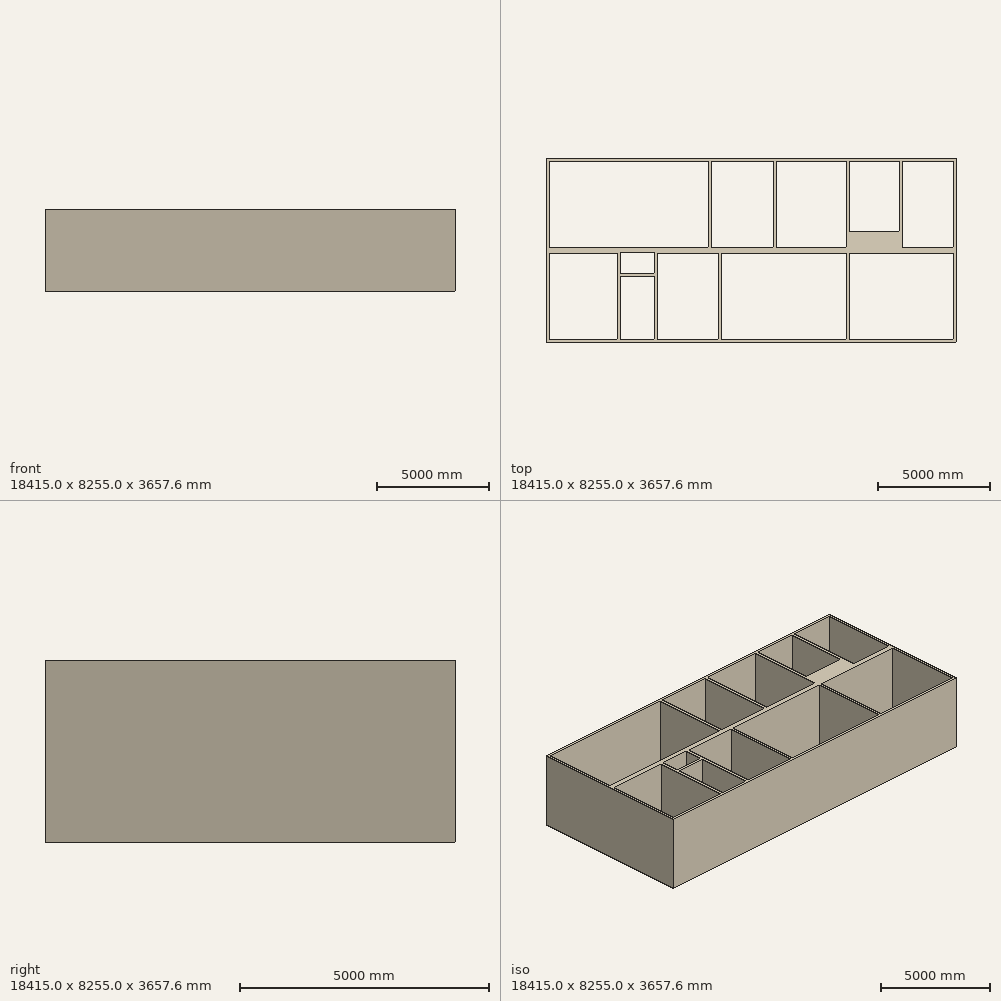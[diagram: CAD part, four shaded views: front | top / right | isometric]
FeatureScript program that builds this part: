
annotation { "Feature Type Name" : "Feature", "Feature Type Description" : "" }
export const myFeature = defineFeature(function(context is Context, id is Id, definition is map)
    precondition{}
    {
        {
            var Q0;
            Q0=qCreatedBy(makeId("Top.planeOp"),FACE);
            var sketch = newSketch(context, id + "F0", { "sketchPlane" : qUnion([Q0])});
            skLineSegment(sketch, "E0.bottom", {"start": v(0, 0) * mm, "end": v(3073.4, 0) * mm});
            skLineSegment(sketch, "E0.top", {"start": v(0, 3860.8) * mm, "end": v(3073.4, 3860.8) * mm});
            skLineSegment(sketch, "E0.left", {"start": v(0, 0) * mm, "end": v(0, 3860.8) * mm});
            skLineSegment(sketch, "E0.right", {"start": v(3073.4, 0) * mm, "end": v(3073.4, 3860.8) * mm});
            skLineSegment(sketch, "E1.bottom", {"start": v(3208.87, 0) * mm, "end": v(4732.87, 0) * mm});
            skLineSegment(sketch, "E1.top", {"start": v(3208.87, 2819.4) * mm, "end": v(4732.87, 2819.4) * mm});
            skLineSegment(sketch, "E1.left", {"start": v(3208.87, 0) * mm, "end": v(3208.87, 2819.4) * mm});
            skLineSegment(sketch, "E1.right", {"start": v(4732.87, 0) * mm, "end": v(4732.87, 2819.4) * mm});
            skLineSegment(sketch, "E2.bottom", {"start": v(3208.87, 2954.87) * mm, "end": v(4732.87, 2954.87) * mm});
            skLineSegment(sketch, "E2.top", {"start": v(3208.87, 3894.67) * mm, "end": v(4732.87, 3894.67) * mm});
            skLineSegment(sketch, "E2.left", {"start": v(3208.87, 2954.87) * mm, "end": v(3208.87, 3894.67) * mm});
            skLineSegment(sketch, "E2.right", {"start": v(4732.87, 2954.87) * mm, "end": v(4732.87, 3894.67) * mm});
            skLineSegment(sketch, "E3.bottom", {"start": v(4868.33, 0) * mm, "end": v(7611.53, 0) * mm});
            skLineSegment(sketch, "E3.top", {"start": v(4868.33, 3860.8) * mm, "end": v(7611.53, 3860.8) * mm});
            skLineSegment(sketch, "E3.left", {"start": v(4868.33, 0) * mm, "end": v(4868.33, 3860.8) * mm});
            skLineSegment(sketch, "E3.right", {"start": v(7611.53, 0) * mm, "end": v(7611.53, 3860.8) * mm});
            skLineSegment(sketch, "E4.bottom", {"start": v(7747, 0) * mm, "end": v(13360.4, 0) * mm});
            skLineSegment(sketch, "E4.top", {"start": v(7747, 3860.8) * mm, "end": v(13360.4, 3860.8) * mm});
            skLineSegment(sketch, "E4.left", {"start": v(7747, 0) * mm, "end": v(7747, 3860.8) * mm});
            skLineSegment(sketch, "E4.right", {"start": v(13360.4, 0) * mm, "end": v(13360.4, 3860.8) * mm});
            skLineSegment(sketch, "E5.bottom", {"start": v(13495.87, 0) * mm, "end": v(18144.07, 0) * mm});
            skLineSegment(sketch, "E5.top", {"start": v(13495.87, 3860.8) * mm, "end": v(18144.07, 3860.8) * mm});
            skLineSegment(sketch, "E5.left", {"start": v(13495.87, 0) * mm, "end": v(13495.87, 3860.8) * mm});
            skLineSegment(sketch, "E5.right", {"start": v(18144.07, 0) * mm, "end": v(18144.07, 3860.8) * mm});
            skLineSegment(sketch, "E6.bottom", {"start": v(18144.07, 4123.27) * mm, "end": v(15858.07, 4123.27) * mm});
            skLineSegment(sketch, "E6.top", {"start": v(18144.07, 7984.07) * mm, "end": v(15858.07, 7984.07) * mm});
            skLineSegment(sketch, "E6.left", {"start": v(18144.07, 4123.27) * mm, "end": v(18144.07, 7984.07) * mm});
            skLineSegment(sketch, "E6.right", {"start": v(15858.07, 4123.27) * mm, "end": v(15858.07, 7984.07) * mm});
            skLineSegment(sketch, "E7.bottom", {"start": v(15722.6, 7984.07) * mm, "end": v(13487.4, 7984.07) * mm});
            skLineSegment(sketch, "E7.top", {"start": v(15722.6, 4841.01) * mm, "end": v(13487.4, 4841.01) * mm});
            skLineSegment(sketch, "E7.left", {"start": v(15722.6, 7984.07) * mm, "end": v(15722.6, 4841.01) * mm});
            skLineSegment(sketch, "E7.right", {"start": v(13487.4, 7984.07) * mm, "end": v(13487.4, 4841.01) * mm});
            skLineSegment(sketch, "E8.bottom", {"start": v(13351.93, 7984.07) * mm, "end": v(10202.33, 7984.07) * mm});
            skLineSegment(sketch, "E8.top", {"start": v(13351.93, 4123.27) * mm, "end": v(10202.33, 4123.27) * mm});
            skLineSegment(sketch, "E8.left", {"start": v(13351.93, 7984.07) * mm, "end": v(13351.93, 4123.27) * mm});
            skLineSegment(sketch, "E8.right", {"start": v(10202.33, 7984.07) * mm, "end": v(10202.33, 4123.27) * mm});
            skLineSegment(sketch, "E9.bottom", {"start": v(10066.87, 7984.07) * mm, "end": v(7272.87, 7984.07) * mm});
            skLineSegment(sketch, "E9.top", {"start": v(10066.87, 4123.27) * mm, "end": v(7272.87, 4123.27) * mm});
            skLineSegment(sketch, "E9.left", {"start": v(10066.87, 7984.07) * mm, "end": v(10066.87, 4123.27) * mm});
            skLineSegment(sketch, "E9.right", {"start": v(7272.87, 7984.07) * mm, "end": v(7272.87, 4123.27) * mm});
            skLineSegment(sketch, "E10.bottom", {"start": v(7137.4, 7984.07) * mm, "end": v(0, 7984.07) * mm});
            skLineSegment(sketch, "E10.top", {"start": v(7137.4, 4123.27) * mm, "end": v(0, 4123.27) * mm});
            skLineSegment(sketch, "E10.left", {"start": v(7137.4, 7984.07) * mm, "end": v(7137.4, 4123.27) * mm});
            skLineSegment(sketch, "E10.right", {"start": v(0, 7984.07) * mm, "end": v(0, 4123.27) * mm});
            skLineSegment(sketch, "E11", {"start": v(3073.4, 0) * mm, "end": v(3208.87, 0) * mm});
            skLineSegment(sketch, "E12", {"start": v(4732.87, 0) * mm, "end": v(4868.33, 0) * mm});
            skLineSegment(sketch, "E13", {"start": v(7611.53, 0) * mm, "end": v(7747, 0) * mm});
            skLineSegment(sketch, "E14", {"start": v(13360.4, 0) * mm, "end": v(13495.87, 0) * mm});
            skLineSegment(sketch, "E15.bottom", {"start": v(-135.47, -135.47) * mm, "end": v(18279.53, -135.47) * mm});
            skLineSegment(sketch, "E15.top", {"start": v(-135.47, 8119.53) * mm, "end": v(18279.53, 8119.53) * mm});
            skLineSegment(sketch, "E15.left", {"start": v(-135.47, -135.47) * mm, "end": v(-135.47, 8119.53) * mm});
            skLineSegment(sketch, "E15.right", {"start": v(18279.53, -135.47) * mm, "end": v(18279.53, 8119.53) * mm});
            skLineSegment(sketch, "E16", {"start": v(3208.87, 2954.87) * mm, "end": v(3208.87, 2819.4) * mm});
            skLineSegment(sketch, "E17", {"start": v(7137.4, 7984.07) * mm, "end": v(7272.87, 7984.07) * mm});
            skLineSegment(sketch, "E18", {"start": v(10066.87, 7984.07) * mm, "end": v(10202.33, 7984.07) * mm});
            skLineSegment(sketch, "E19", {"start": v(13351.93, 7984.07) * mm, "end": v(13487.4, 7984.07) * mm});
            skLineSegment(sketch, "E20", {"start": v(15722.6, 7984.07) * mm, "end": v(15858.07, 7984.07) * mm});
            skLineSegment(sketch, "E21", {"start": v(0, 0) * mm, "end": v(-135.47, 0) * mm});
            skLineSegment(sketch, "E22", {"start": v(0, -135.47) * mm, "end": v(0, 0) * mm});
            skLineSegment(sketch, "E23", {"start": v(0, 7984.07) * mm, "end": v(0, 8119.53) * mm});
            skLineSegment(sketch, "E24", {"start": v(18144.07, 0) * mm, "end": v(18279.53, 0) * mm});
            skSolve(sketch);
        }
        {
            var Q0;
            Q0=makeQuery(id+"F0.imprint","IMPRINT",FACE,{"disambiguationData":[TD([[makeQuery(id+"F0.imprint","IMPRINT",EDGE,{"derivedFrom":sQuery(id+"F0.wireOp",EDGE,"E0.top")}),1.0]])]});
            var Q1;
            {var subQ4=sQuery(id+"F0.wireOp",EDGE,"E21");Q1=makeQuery(id+"F0.imprint","IMPRINT",FACE,{"disambiguationData":[TD([[makeQuery(id+"F0.imprint","IMPRINT",EDGE,{"derivedFrom":subQ4}),1.0]])]});}
            var Q2;
            Q2=makeQuery(id+"F0.imprint","IMPRINT",FACE,{"disambiguationData":[TD([[makeQuery(id+"F0.imprint","IMPRINT",EDGE,{"derivedFrom":sQuery(id+"F0.wireOp",EDGE,"E0.bottom")}),-1.0]])]});
            extrude(context, id + "F1", {"entities" : qUnion([Q0, Q1, Q2]), "depth" : 3657.6 * mm, "offsetDistance" : 30.48 * mm});
        }
    });
